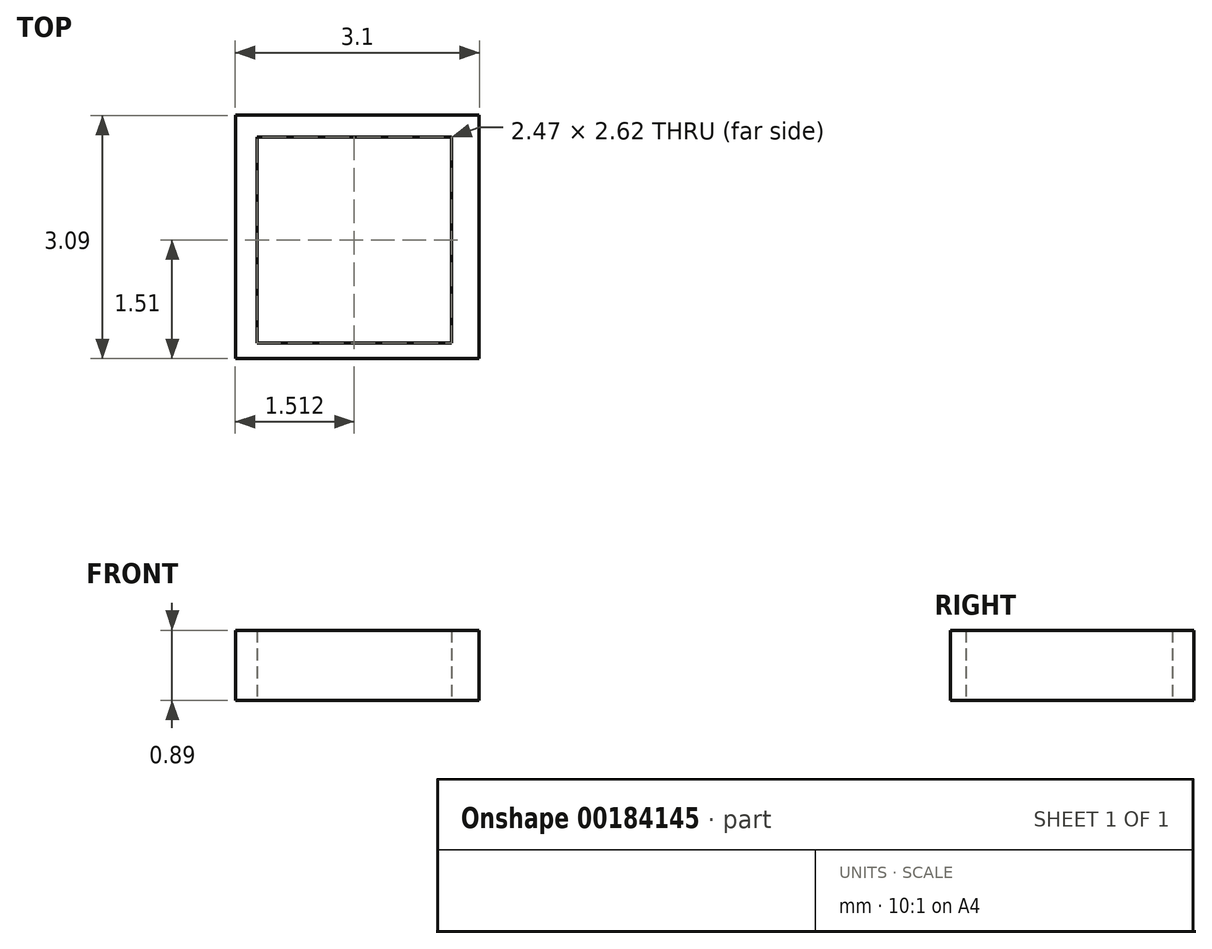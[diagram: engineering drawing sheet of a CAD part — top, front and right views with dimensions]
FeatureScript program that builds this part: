
annotation { "Feature Type Name" : "Feature", "Feature Type Description" : "" }
export const myFeature = defineFeature(function(context is Context, id is Id, definition is map)
    precondition{}
    {
        {
            var Q0;
            Q0=qCreatedBy(makeId("Top.planeOp"),FACE);
            var sketch = newSketch(context, id + "F0", { "sketchPlane" : qUnion([Q0])});
            skLineSegment(sketch, "E0.bottom", {"start": v(-20.72, 6.85) * mm, "end": v(-18.24, 6.85) * mm});
            skLineSegment(sketch, "E0.top", {"start": v(-20.72, 4.23) * mm, "end": v(-18.24, 4.23) * mm});
            skLineSegment(sketch, "E0.left", {"start": v(-20.72, 6.85) * mm, "end": v(-20.72, 4.23) * mm});
            skLineSegment(sketch, "E0.right", {"start": v(-18.24, 6.85) * mm, "end": v(-18.24, 4.23) * mm});
            skLineSegment(sketch, "E1.bottom", {"start": v(-20.99, 7.12) * mm, "end": v(-17.9, 7.12) * mm});
            skLineSegment(sketch, "E1.top", {"start": v(-20.99, 4.03) * mm, "end": v(-17.9, 4.03) * mm});
            skLineSegment(sketch, "E1.left", {"start": v(-20.99, 7.12) * mm, "end": v(-20.99, 4.03) * mm});
            skLineSegment(sketch, "E1.right", {"start": v(-17.9, 7.12) * mm, "end": v(-17.9, 4.03) * mm});
            skSolve(sketch);
        }
        {
            var Q0;
            Q0 = qSketchRegion(id + "F0", true);
            extrude(context, id + "F1", {"entities" : qUnion([Q0]), "depth" : 0.89 * mm});
        }
    });
